# Revit family: QF_COMENDA_CE68
name_source: partatom
category: Attrezzature speciali
units: mm (PartAtom-declared; Revit-internal decimal feet)

## family parameters
Basato su piano di lavoro = No
Condiviso = No
Numero OmniClass = 23.40.40.14
Punto di calcolo locali = No
Quota connettore circolare = Usa diametro
Sempre verticale = Sì
Taglio con vuoti quando caricato = No
Tipo di parte = Normale
Titolo OmniClass = Food Service Equipment

## types (3) — shared parameters
Accessorio = No
Altezza = 830 mm  [stored 2.7231 ft]
Assorbimento corrente minimo = 0 A
Cavo di allacciamento compreso nella fornitura = No
Corrente a pieno carico = 11 A
Diametro di scarico indiretto acqua = 51 mm
Diametro raccordo acqua calda = 19 mm
Fase = 3
Frequenza = 50 Hz
Lunghezza = 600 mm
Numero dei poli = 3
Peso netto = 0.00 kg
Portata acqua calda = 0.0 L/s
Potenza apparente = 7830 VA
Potenza elettrica = 7830 W
Produttore = HOONVED
Profondità = 695 mm  [stored 2.28018 ft]
Protezione contro le sovracorrenti = 0 A
Temperatura di alimentazione acqua calda = 0 °C
Temperatura raccomandata per acqua calda  = 0 °C
Tensione = 400 V
URL = https://www.hoonved.com
URL catalogo = https://www.hoonved.com
zero-valued in all types: Costo

## per-type parameters (varying)
| type | Descrizione | Modello |
| H56525 | MULTIPURPOSE WASHER 500X600 MM RACK SIZE | CE68 |
| H56526 | MULTIPURPOSE WASHER 500X600 MM RACK SIZE WITH WATER SOFTENER | CE68D |
| H56527 | MULTIPURPOSE WASHER 500X600 MM RACK SIZE WITH BREAK TANK | CE68D |

note: [stored X ft] marks values corroborated as IEEE doubles in the binary element streams (Revit-internal decimal feet)

## geometry (parser evidence)
native form markers: Sweep x3
no freeform markers — native parametric forms only
